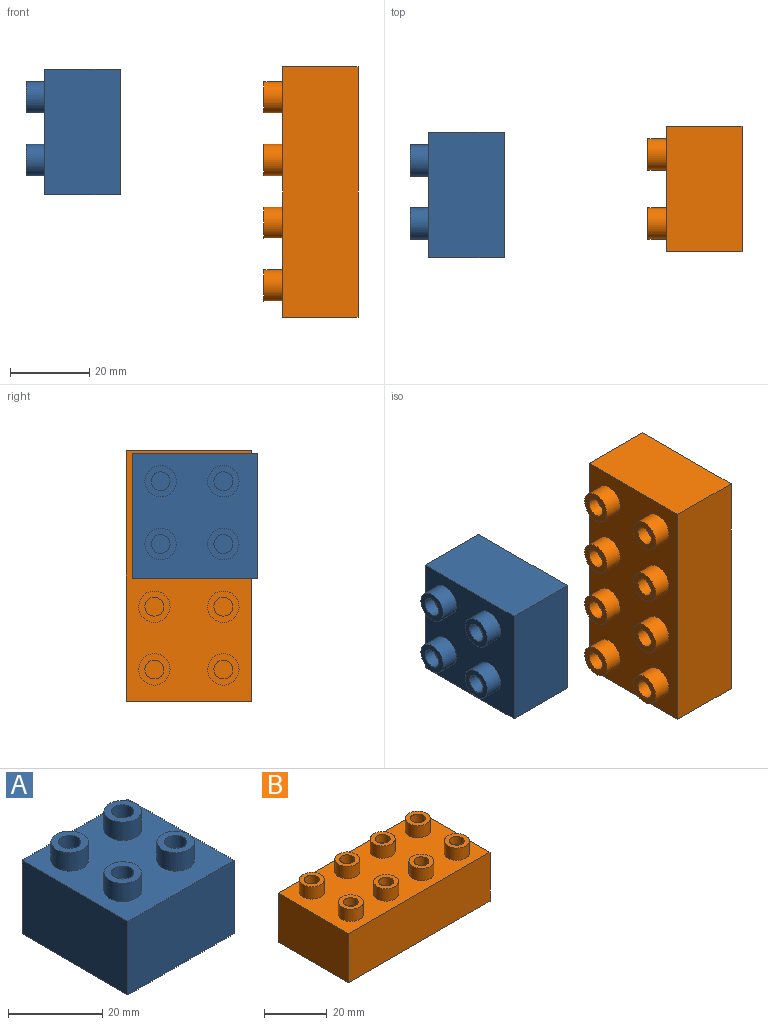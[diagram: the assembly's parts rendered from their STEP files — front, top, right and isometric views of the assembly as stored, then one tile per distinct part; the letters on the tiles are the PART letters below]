
ASSEMBLY  parts=2 mates=1
PART A: 27 faces, bbox 31.8x31.8x23.8 mm
  f0: plane 31.75x19.05mm, normal (1,0,0), area 604.8mm2, adj f1,f3,f4,f5
  f1: plane 31.75x19.05mm, normal (0,1,0), area 604.8mm2, adj f0,f2,f4,f5
  f2: plane 31.75x19.05mm, normal (-1,0,0), area 604.8mm2, adj f1,f3,f4,f5
  f3: plane 31.75x19.05mm, normal (0,-1,0), area 604.8mm2, adj f0,f2,f4,f5
  f4: plane 31.75x31.75mm, normal (0,0,1), area 810.1mm2, adj f0,f1,f2,f3,f11,f13,f15,f17
  f5: plane 31.75x31.75mm, normal (0,0,-1), area 191.5mm2, adj f0,f1,f2,f3,f6,f7,f8,f9
  f6: plane 28.58x17.46mm, normal (-1,0,0), area 499mm2, adj f5,f7,f9,f10
  f7: plane 28.58x17.46mm, normal (0,-1,0), area 499mm2, adj f5,f6,f8,f10
  f8: plane 28.58x17.46mm, normal (1,0,0), area 499mm2, adj f5,f7,f9,f10
  f9: plane 28.58x17.46mm, normal (0,1,0), area 499mm2, adj f5,f6,f8,f10
  f10: plane 28.58x28.58mm, normal (0,0,-1), area 816.5mm2, adj f6,f7,f8,f9
  f11: cylinder r=3.97mm len=7.94mm, axis (0,0,-1), area 118.8mm2, adj f4,f12
  f12: plane 7.94x7.94mm, normal (0,0,1), area 31.7mm2, adj f11,f19
  f13: cylinder r=3.97mm len=7.94mm, axis (0,0,-1), area 118.8mm2, adj f4,f14
  f14: plane 7.94x7.94mm, normal (0,0,1), area 31.7mm2, adj f13,f21
  f15: cylinder r=3.97mm len=7.94mm, axis (0,0,-1), area 118.8mm2, adj f4,f16
  f16: plane 7.94x7.94mm, normal (0,0,1), area 31.7mm2, adj f15,f23
  f17: cylinder r=3.97mm len=7.94mm, axis (0,0,-1), area 118.8mm2, adj f4,f18
  f18: plane 7.94x7.94mm, normal (0,0,1), area 31.7mm2, adj f17,f25
  f19: cylinder r=2.38mm len=4.76mm, axis (0,0,1), area 47.5mm2, adj f12,f20
  f20: plane 4.76x4.76mm, normal (0,0,1), area 17.8mm2, adj f19
  f21: cylinder r=2.38mm len=4.76mm, axis (0,0,1), area 47.5mm2, adj f14,f22
  f22: plane 4.76x4.76mm, normal (0,0,1), area 17.8mm2, adj f21
  f23: cylinder r=2.38mm len=4.76mm, axis (0,0,1), area 47.5mm2, adj f16,f24
  f24: plane 4.76x4.76mm, normal (0,0,1), area 17.8mm2, adj f23
  f25: cylinder r=2.38mm len=4.76mm, axis (0,0,1), area 47.5mm2, adj f18,f26
  f26: plane 4.76x4.76mm, normal (0,0,1), area 17.8mm2, adj f25
PART B: 43 faces, bbox 63.5x31.8x23.8 mm
  f0: plane 31.75x19.05mm, normal (1,0,0), area 604.8mm2, adj f1,f3,f4,f5
  f1: plane 63.5x19.05mm, normal (0,1,0), area 1209.7mm2, adj f0,f2,f4,f5
  f2: plane 31.75x19.05mm, normal (-1,0,0), area 604.8mm2, adj f1,f3,f4,f5
  f3: plane 63.5x19.05mm, normal (0,-1,0), area 1209.7mm2, adj f0,f2,f4,f5
  f4: plane 63.5x31.75mm, normal (0,0,1), area 1620.3mm2, adj f0,f1,f2,f3,f11,f13,f15,f17
  f5: plane 63.5x31.75mm, normal (0,0,-1), area 292.3mm2, adj f0,f1,f2,f3,f6,f7,f8,f9
  f6: plane 28.58x17.46mm, normal (-1,0,0), area 499mm2, adj f5,f7,f9,f10
  f7: plane 60.33x17.46mm, normal (0,-1,0), area 1053.4mm2, adj f5,f6,f8,f10
  f8: plane 28.58x17.46mm, normal (1,0,0), area 499mm2, adj f5,f7,f9,f10
  f9: plane 60.33x17.46mm, normal (0,1,0), area 1053.4mm2, adj f5,f6,f8,f10
  f10: plane 60.33x28.58mm, normal (0,0,-1), area 1723.8mm2, adj f6,f7,f8,f9
  f11: cylinder r=3.97mm len=7.94mm, axis (0,0,-1), area 118.8mm2, adj f4,f12
  f12: plane 7.94x7.94mm, normal (0,0,1), area 31.7mm2, adj f11,f27
  f13: cylinder r=3.97mm len=7.94mm, axis (0,0,-1), area 118.8mm2, adj f4,f14
  f14: plane 7.94x7.94mm, normal (0,0,1), area 31.7mm2, adj f13,f29
  f15: cylinder r=3.97mm len=7.94mm, axis (0,0,-1), area 118.8mm2, adj f4,f16
  f16: plane 7.94x7.94mm, normal (0,0,1), area 31.7mm2, adj f15,f31
  f17: cylinder r=3.97mm len=7.94mm, axis (0,0,-1), area 118.8mm2, adj f4,f18
  f18: plane 7.94x7.94mm, normal (0,0,1), area 31.7mm2, adj f17,f33
  f19: cylinder r=3.97mm len=7.94mm, axis (0,0,-1), area 118.8mm2, adj f4,f20
  f20: plane 7.94x7.94mm, normal (0,0,1), area 31.7mm2, adj f19,f35
  f21: cylinder r=3.97mm len=7.94mm, axis (0,0,-1), area 118.8mm2, adj f4,f22
  f22: plane 7.94x7.94mm, normal (0,0,1), area 31.7mm2, adj f21,f37
  f23: cylinder r=3.97mm len=7.94mm, axis (0,0,-1), area 118.8mm2, adj f4,f24
  f24: plane 7.94x7.94mm, normal (0,0,1), area 31.7mm2, adj f23,f39
  f25: cylinder r=3.97mm len=7.94mm, axis (0,0,-1), area 118.8mm2, adj f4,f26
  f26: plane 7.94x7.94mm, normal (0,0,1), area 31.7mm2, adj f25,f41
  f27: cylinder r=2.38mm len=4.76mm, axis (0,0,1), area 47.5mm2, adj f12,f28
  f28: plane 4.76x4.76mm, normal (0,0,1), area 17.8mm2, adj f27
  f29: cylinder r=2.38mm len=4.76mm, axis (0,0,1), area 47.5mm2, adj f14,f30
  f30: plane 4.76x4.76mm, normal (0,0,1), area 17.8mm2, adj f29
  f31: cylinder r=2.38mm len=4.76mm, axis (0,0,1), area 47.5mm2, adj f16,f32
  f32: plane 4.76x4.76mm, normal (0,0,1), area 17.8mm2, adj f31
  f33: cylinder r=2.38mm len=4.76mm, axis (0,0,1), area 47.5mm2, adj f18,f34
  f34: plane 4.76x4.76mm, normal (0,0,1), area 17.8mm2, adj f33
  f35: cylinder r=2.38mm len=4.76mm, axis (0,0,1), area 47.5mm2, adj f20,f36
  f36: plane 4.76x4.76mm, normal (0,0,1), area 17.8mm2, adj f35
  f37: cylinder r=2.38mm len=4.76mm, axis (0,0,1), area 47.5mm2, adj f22,f38
  f38: plane 4.76x4.76mm, normal (0,0,1), area 17.8mm2, adj f37
  f39: cylinder r=2.38mm len=4.76mm, axis (0,0,1), area 47.5mm2, adj f24,f40
  f40: plane 4.76x4.76mm, normal (0,0,1), area 17.8mm2, adj f39
  f41: cylinder r=2.38mm len=4.76mm, axis (0,0,1), area 47.5mm2, adj f26,f42
  f42: plane 4.76x4.76mm, normal (0,0,1), area 17.8mm2, adj f41
PLACE A rot(axis=(0.58,-0.58,-0.58),120deg) t=(-52.27,-1.59,16.64)mm
PLACE B rot(axis=(0,-1,0),90deg) t=(7.94,1.4,0)mm
MATE slider A.f17 <-> B.f23  axis (-1,0,0) through (-61.8,-8.73,8.1)mm
